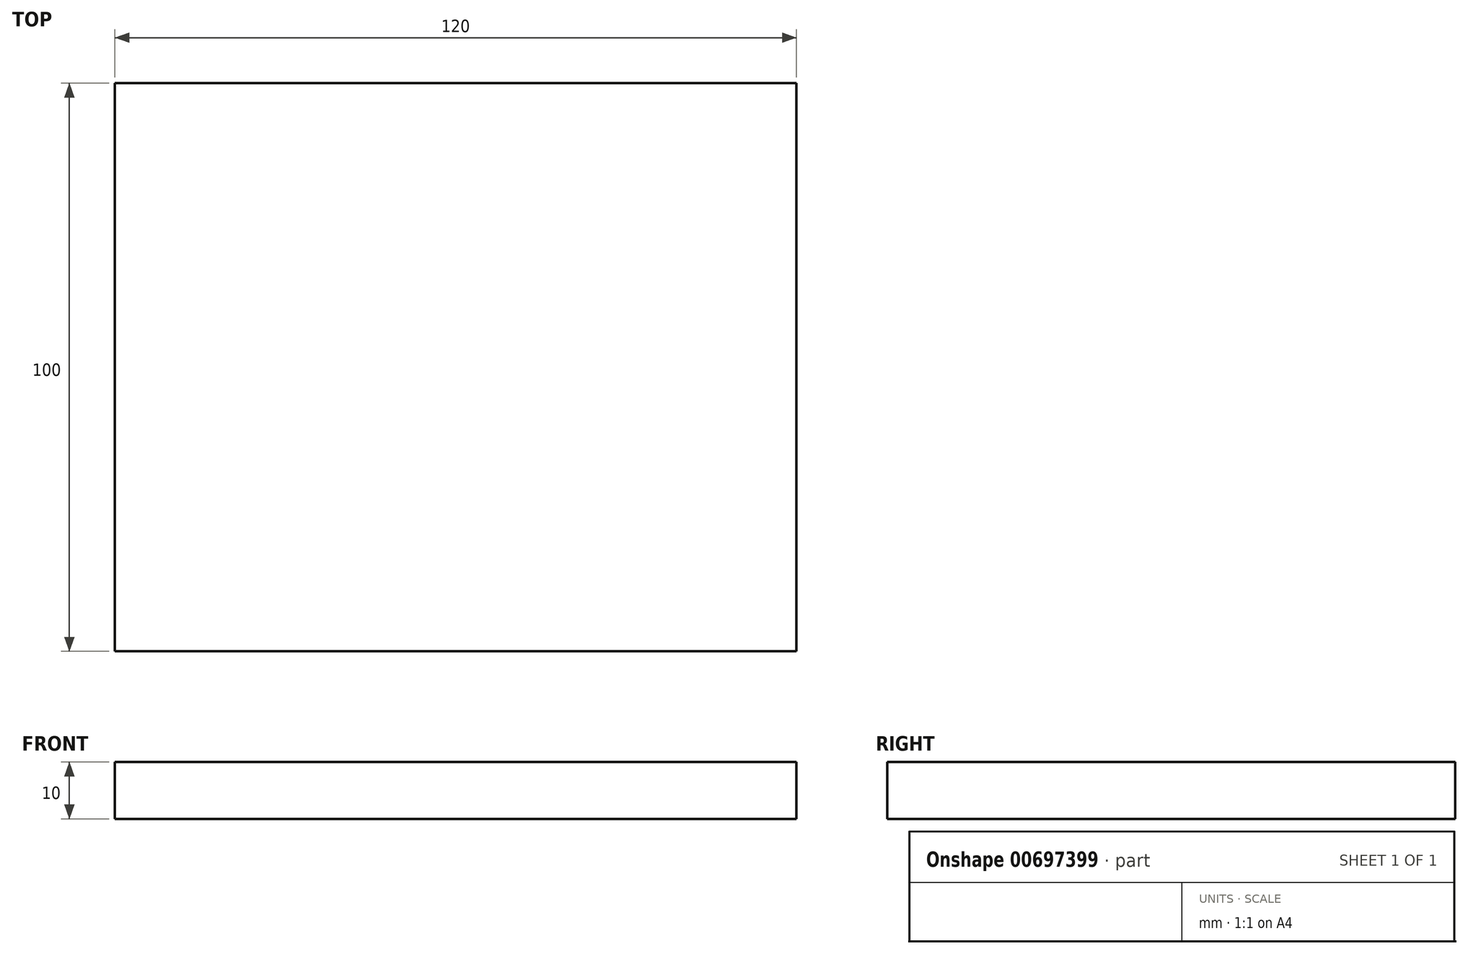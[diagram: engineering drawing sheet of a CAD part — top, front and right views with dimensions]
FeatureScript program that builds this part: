
annotation { "Feature Type Name" : "Feature", "Feature Type Description" : "" }
export const myFeature = defineFeature(function(context is Context, id is Id, definition is map)
    precondition{}
    {
        {
            var Q0;
            Q0=qCreatedBy(makeId("Top.planeOp"),FACE);
            var sketch = newSketch(context, id + "F0", { "sketchPlane" : qUnion([Q0])});
            skLineSegment(sketch, "E0.bottom", {"start": v(-60, 50) * mm, "end": v(60, 50) * mm});
            skLineSegment(sketch, "E0.top", {"start": v(-60, -50) * mm, "end": v(60, -50) * mm});
            skLineSegment(sketch, "E0.left", {"start": v(-60, 50) * mm, "end": v(-60, -50) * mm});
            skLineSegment(sketch, "E0.right", {"start": v(60, 50) * mm, "end": v(60, -50) * mm});
            skPoint(sketch, "E0.middle", {"position": v(0, 0) * mm});
            skSolve(sketch);
        }
        {
            var Q0;
            Q0=makeQuery(id+"F0.imprint","IMPRINT",FACE,{"disambiguationData":[TD([[makeQuery(id+"F0.imprint","IMPRINT",EDGE,{"derivedFrom":sQuery(id+"F0.wireOp",EDGE,"E0.bottom")}),-1.0]])]});
            extrude(context, id + "F1", {"entities" : qUnion([Q0]), "oppositeDirection" : true, "depth" : 10 * mm, "offsetDistance" : 25 * mm});
        }
    });
